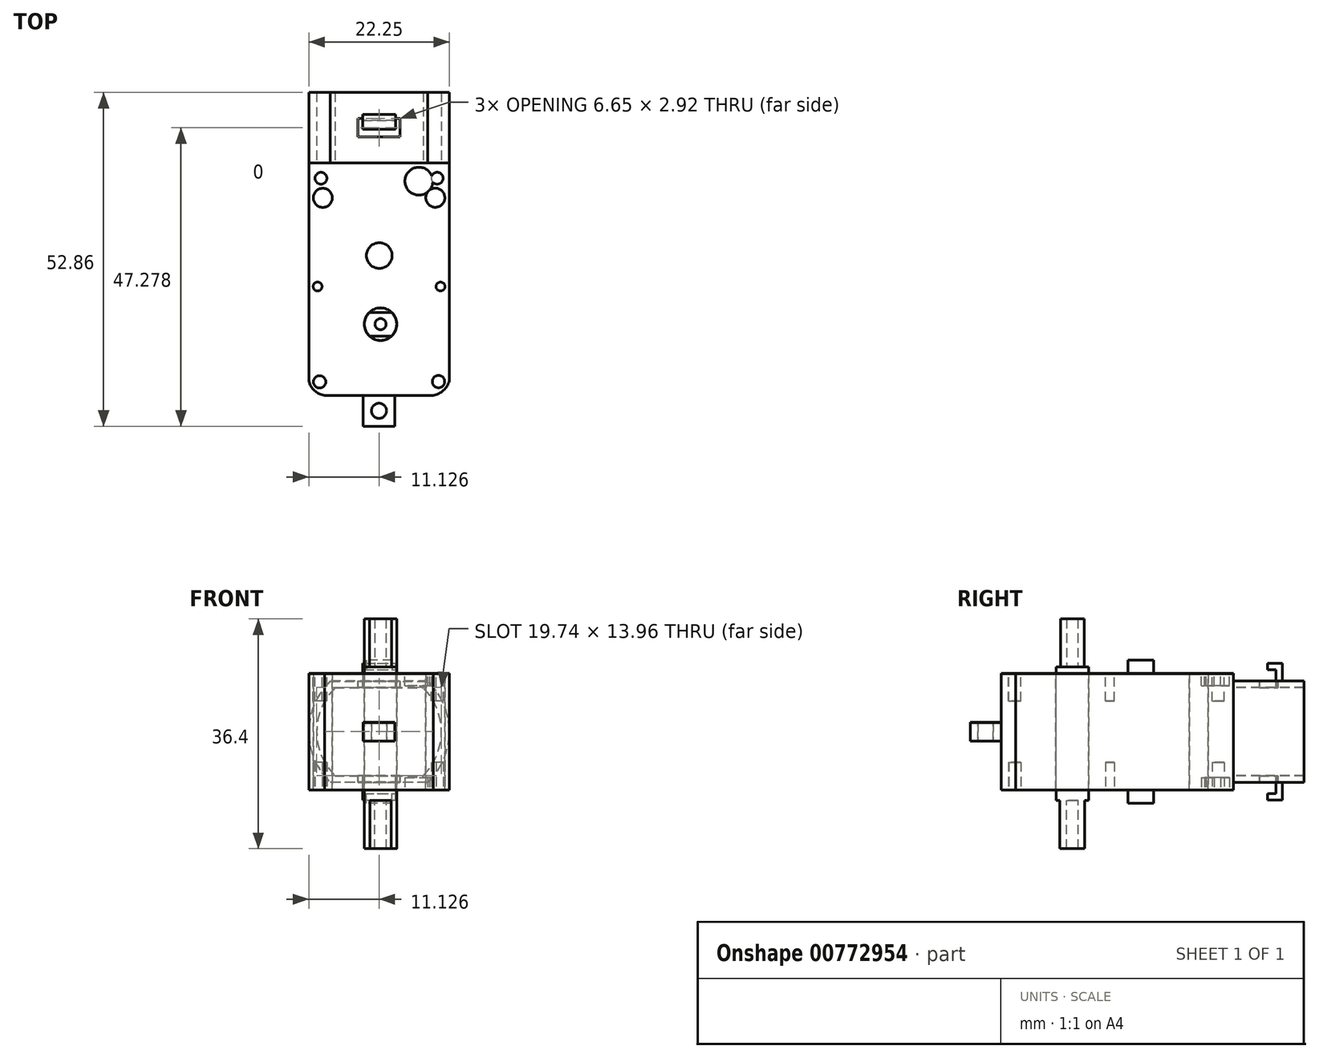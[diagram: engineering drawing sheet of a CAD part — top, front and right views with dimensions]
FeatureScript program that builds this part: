
annotation { "Feature Type Name" : "Feature", "Feature Type Description" : "" }
export const myFeature = defineFeature(function(context is Context, id is Id, definition is map)
    precondition{}
    {
        {
            var Q0;
            Q0=qCreatedBy(makeId("Top.planeOp"),FACE);
            var sketch = newSketch(context, id + "F0", { "sketchPlane" : qUnion([Q0])});
            skLineSegment(sketch, "E0.bottom", {"start": v(-45.26, 0.57) * mm, "end": v(-23, 0.57) * mm});
            skLineSegment(sketch, "E0.top", {"start": v(-42.73, -36.23) * mm, "end": v(-25.55, -36.23) * mm});
            skLineSegment(sketch, "E0.left", {"start": v(-45.26, 0.57) * mm, "end": v(-45.26, -33.94) * mm});
            skLineSegment(sketch, "E0.right", {"start": v(-23, 0.57) * mm, "end": v(-23, -33.94) * mm});
            skCircle(sketch, "E1", {"center": v(-25.23, -4.93) * mm, "radius": 1.51 * mm});
            skCircle(sketch, "E2", {"center": v(-43.04, -4.94) * mm, "radius": 1.51 * mm});
            skArc(sketch, "E3", {"start": v(-45.26, -33.94) * mm, "mid": v(-44.35, -35.48) * mm, "end": v(-42.73, -36.23) * mm});
            skArc(sketch, "E4", {"start": v(-25.55, -36.23) * mm, "mid": v(-23.95, -35.45) * mm, "end": v(-23, -33.94) * mm});
            skCircle(sketch, "E5", {"center": v(-33.9, -24.96) * mm, "radius": 2.58 * mm});
            skLineSegment(sketch, "E6", {"start": v(-25.39, -3.43) * mm, "end": v(-43.04, -3.43) * mm});
            skSolve(sketch);
        }
        {
            var Q0;
            Q0=makeQuery(id+"F0.imprint","IMPRINT",FACE,{"disambiguationData":[TD([[makeQuery(id+"F0.imprint","IMPRINT",EDGE,{"derivedFrom":sQuery(id+"F0.wireOp",EDGE,"E0.bottom")}),-1.0]])]});
            extrude(context, id + "F1", {"entities" : qUnion([Q0]), "depth" : 18.45 * mm, "offsetDistance" : 25.4 * mm});
        }
        {
            var Q0;
            Q0=makeQuery(id+"F1.opExtrude","CAP_FACE",FACE,{"disambiguationData":[OSD([sQuery(id+"F0.wireOp",EDGE,"E0.bottom"),sQuery(id+"F0.wireOp",EDGE,"E0.top"),sQuery(id+"F0.wireOp",EDGE,"E0.left"),sQuery(id+"F0.wireOp",EDGE,"E0.right"),sQuery(id+"F0.wireOp",EDGE,"E1"),sQuery(id+"F0.wireOp",EDGE,"E2"),sQuery(id+"F0.wireOp",EDGE,"E3"),sQuery(id+"F0.wireOp",EDGE,"E4"),sQuery(id+"F0.wireOp",EDGE,"E5")])],"isStart":false});
            var sketch = newSketch(context, id + "F2", { "sketchPlane" : qUnion([Q0])});
            skCircle(sketch, "E7", {"center": v(-34.1, -14.09) * mm, "radius": 2.03 * mm});
            skSolve(sketch);
        }
        {
            var Q0;
            Q0=makeQuery(id+"F2.imprint","IMPRINT",FACE,{"disambiguationData":[TD([[makeQuery(id+"F2.imprint","IMPRINT",EDGE,{"derivedFrom":sQuery(id+"F2.wireOp",EDGE,"E7")}),1.0]])]});
            extrude(context, id + "F3", {"entities" : qUnion([Q0]), "operationType" : NewBodyOperationType.ADD, "depth" : 2.08 * mm, "offsetDistance" : 25.4 * mm});
        }
        {
            var Q0;
            Q0=makeQuery(id+"F1.opExtrude","CAP_FACE",FACE,{"disambiguationData":[OSD([sQuery(id+"F0.wireOp",EDGE,"E0.bottom"),sQuery(id+"F0.wireOp",EDGE,"E0.top"),sQuery(id+"F0.wireOp",EDGE,"E0.left"),sQuery(id+"F0.wireOp",EDGE,"E0.right"),sQuery(id+"F0.wireOp",EDGE,"E1"),sQuery(id+"F0.wireOp",EDGE,"E2"),sQuery(id+"F0.wireOp",EDGE,"E3"),sQuery(id+"F0.wireOp",EDGE,"E4"),sQuery(id+"F0.wireOp",EDGE,"E5")])],"isStart":false});
            var sketch = newSketch(context, id + "F4", { "sketchPlane" : qUnion([Q0])});
            skCircle(sketch, "E8", {"center": v(-43.55, -34.1) * mm, "radius": 0.98 * mm});
            skCircle(sketch, "E9", {"center": v(-24.72, -34.04) * mm, "radius": 0.98 * mm});
            skCircle(sketch, "E10", {"center": v(-24.4, -19) * mm, "radius": 0.71 * mm});
            skCircle(sketch, "E11", {"center": v(-24.93, -1.84) * mm, "radius": 0.94 * mm});
            skCircle(sketch, "E12", {"center": v(-43.86, -19) * mm, "radius": 0.71 * mm});
            skCircle(sketch, "E13", {"center": v(-43.33, -1.84) * mm, "radius": 0.94 * mm});
            skCircle(sketch, "E14", {"center": v(-39.93, -1.7) * mm, "radius": 1.61 * mm});
            skCircle(sketch, "E15", {"center": v(-28.78, -0.73) * mm, "radius": 0.33 * mm});
            skSolve(sketch);
        }
        {
            var Q0;
            Q0=makeQuery(id+"F4.imprint","IMPRINT",FACE,{"disambiguationData":[TD([[makeQuery(id+"F4.imprint","IMPRINT",EDGE,{"derivedFrom":sQuery(id+"F4.wireOp",EDGE,"E13")}),1.0]])]});
            var Q1;
            Q1=makeQuery(id+"F4.imprint","IMPRINT",FACE,{"disambiguationData":[TD([[makeQuery(id+"F4.imprint","IMPRINT",EDGE,{"derivedFrom":sQuery(id+"F4.wireOp",EDGE,"E12")}),1.0]])]});
            var Q2;
            Q2=makeQuery(id+"F4.imprint","IMPRINT",FACE,{"disambiguationData":[TD([[makeQuery(id+"F4.imprint","IMPRINT",EDGE,{"derivedFrom":sQuery(id+"F4.wireOp",EDGE,"E8")}),1.0]])]});
            var Q3;
            Q3=makeQuery(id+"F4.imprint","IMPRINT",FACE,{"disambiguationData":[TD([[makeQuery(id+"F4.imprint","IMPRINT",EDGE,{"derivedFrom":sQuery(id+"F4.wireOp",EDGE,"E9")}),1.0]])]});
            var Q4;
            Q4=makeQuery(id+"F4.imprint","IMPRINT",FACE,{"disambiguationData":[TD([[makeQuery(id+"F4.imprint","IMPRINT",EDGE,{"derivedFrom":sQuery(id+"F4.wireOp",EDGE,"E10")}),1.0]])]});
            var Q5;
            Q5=makeQuery(id+"F4.imprint","IMPRINT",FACE,{"disambiguationData":[TD([[makeQuery(id+"F4.imprint","IMPRINT",EDGE,{"derivedFrom":sQuery(id+"F4.wireOp",EDGE,"E11")}),1.0]])]});
            extrude(context, id + "F5", {"entities" : qUnion([Q0, Q1, Q2, Q3, Q4, Q5]), "operationType" : NewBodyOperationType.REMOVE, "oppositeDirection" : true, "depth" : 4.4 * mm, "offsetDistance" : 25.4 * mm});
        }
        {
            var Q0;
            Q0=makeQuery(id+"F1.opExtrude","CAP_FACE",FACE,{"disambiguationData":[OSD([sQuery(id+"F0.wireOp",EDGE,"E0.bottom"),sQuery(id+"F0.wireOp",EDGE,"E0.top"),sQuery(id+"F0.wireOp",EDGE,"E0.left"),sQuery(id+"F0.wireOp",EDGE,"E0.right"),sQuery(id+"F0.wireOp",EDGE,"E1"),sQuery(id+"F0.wireOp",EDGE,"E2"),sQuery(id+"F0.wireOp",EDGE,"E3"),sQuery(id+"F0.wireOp",EDGE,"E4"),sQuery(id+"F0.wireOp",EDGE,"E5")])],"isStart":false});
            var sketch = newSketch(context, id + "F6", { "sketchPlane" : qUnion([Q0])});
            skCircle(sketch, "E16", {"center": v(-40.43, -2.3) * mm, "radius": 2.2 * mm});
            skCircle(sketch, "E17", {"center": v(-27.83, -2.3) * mm, "radius": 2.2 * mm});
            skSolve(sketch);
        }
        {
            var Q0;
            {var subQ0=sQuery(id+"F6.wireOp",EDGE,"E17");var subQ1=makeQuery(id+"F1.opExtrude","CAP_EDGE",EDGE,{"disambiguationData":[OSD([sQuery(id+"F0.wireOp",EDGE,"E1")])],"isStart":false});var subQ2=makeQuery(id+"F6.imprint","INTERSECT",VERTEX,{"disambiguationData":[OD(0.0)],"derivedFrom":[subQ1,subQ0]});Q0=makeQuery(id+"F6.imprint","IMPRINT",FACE,{"disambiguationData":[TD([[makeQuery(id+"F6.imprint","IMPRINT",EDGE,{"disambiguationData":[TD([[subQ2,1.0]])],"derivedFrom":subQ0}),1.0]])]});}
            var Q1;
            {var subQ0=sQuery(id+"F6.wireOp",EDGE,"E16");var subQ1=makeQuery(id+"F5.boolean.opBoolean","COPY",EDGE,{"derivedFrom":makeQuery(id+"F5.opExtrude","CAP_EDGE",EDGE,{"disambiguationData":[OSD([sQuery(id+"F4.wireOp",EDGE,"E13")])],"isStart":true})});var subQ2=makeQuery(id+"F6.imprint","INTERSECT",VERTEX,{"disambiguationData":[OD(0.0)],"derivedFrom":[subQ1,subQ0]});Q1=makeQuery(id+"F6.imprint","IMPRINT",FACE,{"disambiguationData":[TD([[makeQuery(id+"F6.imprint","IMPRINT",EDGE,{"disambiguationData":[TD([[subQ2,1.0]])],"derivedFrom":subQ0}),1.0]])]});}
            var Q2;
            {var subQ0=sQuery(id+"F6.wireOp",EDGE,"E16");var subQ1=makeQuery(id+"F1.opExtrude","CAP_EDGE",EDGE,{"disambiguationData":[OSD([sQuery(id+"F0.wireOp",EDGE,"E2")])],"isStart":false});var subQ2=makeQuery(id+"F6.imprint","INTERSECT",VERTEX,{"disambiguationData":[OD(0.0)],"derivedFrom":[subQ1,subQ0]});Q2=makeQuery(id+"F6.imprint","IMPRINT",FACE,{"disambiguationData":[TD([[makeQuery(id+"F6.imprint","IMPRINT",EDGE,{"disambiguationData":[TD([[subQ2,-1.0]])],"derivedFrom":subQ0}),1.0]])]});}
            var Q3;
            {var subQ0=sQuery(id+"F6.wireOp",EDGE,"E17");var subQ1=makeQuery(id+"F1.opExtrude","CAP_EDGE",EDGE,{"disambiguationData":[OSD([sQuery(id+"F0.wireOp",EDGE,"E1")])],"isStart":false});var subQ2=makeQuery(id+"F6.imprint","INTERSECT",VERTEX,{"disambiguationData":[OD(0.0)],"derivedFrom":[subQ1,subQ0]});Q3=makeQuery(id+"F6.imprint","IMPRINT",FACE,{"disambiguationData":[TD([[makeQuery(id+"F6.imprint","IMPRINT",EDGE,{"disambiguationData":[TD([[subQ2,-1.0]])],"derivedFrom":subQ0}),1.0]])]});}
            var Q4;
            {var subQ0=sQuery(id+"F6.wireOp",EDGE,"E17");var subQ1=makeQuery(id+"F5.boolean.opBoolean","COPY",EDGE,{"derivedFrom":makeQuery(id+"F5.opExtrude","CAP_EDGE",EDGE,{"disambiguationData":[OSD([sQuery(id+"F4.wireOp",EDGE,"E11")])],"isStart":true})});var subQ2=makeQuery(id+"F6.imprint","INTERSECT",VERTEX,{"disambiguationData":[OD(0.0)],"derivedFrom":[subQ1,subQ0]});Q4=makeQuery(id+"F6.imprint","IMPRINT",FACE,{"disambiguationData":[TD([[makeQuery(id+"F6.imprint","IMPRINT",EDGE,{"disambiguationData":[TD([[subQ2,1.0]])],"derivedFrom":subQ0}),1.0]])]});}
            var Q5;
            {var subQ0=sQuery(id+"F6.wireOp",EDGE,"E16");var subQ1=makeQuery(id+"F5.boolean.opBoolean","COPY",EDGE,{"derivedFrom":makeQuery(id+"F5.opExtrude","CAP_EDGE",EDGE,{"disambiguationData":[OSD([sQuery(id+"F4.wireOp",EDGE,"E13")])],"isStart":true})});var subQ2=makeQuery(id+"F6.imprint","INTERSECT",VERTEX,{"disambiguationData":[OD(0.0)],"derivedFrom":[subQ1,subQ0]});Q5=makeQuery(id+"F6.imprint","IMPRINT",FACE,{"disambiguationData":[TD([[makeQuery(id+"F6.imprint","IMPRINT",EDGE,{"disambiguationData":[TD([[subQ2,-1.0]])],"derivedFrom":subQ0}),1.0]])]});}
            extrude(context, id + "F7", {"entities" : qUnion([Q0, Q1, Q2, Q3, Q4, Q5]), "operationType" : NewBodyOperationType.REMOVE, "oppositeDirection" : true, "depth" : 1.98 * mm, "offsetDistance" : 25.4 * mm});
        }
        {
            var Q0;
            Q0=makeQuery(id+"F1.opExtrude","CAP_FACE",FACE,{"disambiguationData":[OSD([sQuery(id+"F0.wireOp",EDGE,"E0.bottom"),sQuery(id+"F0.wireOp",EDGE,"E0.top"),sQuery(id+"F0.wireOp",EDGE,"E0.left"),sQuery(id+"F0.wireOp",EDGE,"E0.right"),sQuery(id+"F0.wireOp",EDGE,"E1"),sQuery(id+"F0.wireOp",EDGE,"E2"),sQuery(id+"F0.wireOp",EDGE,"E3"),sQuery(id+"F0.wireOp",EDGE,"E4"),sQuery(id+"F0.wireOp",EDGE,"E5")])],"isStart":false});
            var sketch = newSketch(context, id + "F8", { "sketchPlane" : qUnion([Q0])});
            skCircle(sketch, "E18", {"center": v(-33.9, -24.96) * mm, "radius": 2.57 * mm});
            skSolve(sketch);
        }
        {
            var Q0;
            Q0 = qSketchRegion(id + "F8", true);
            extrude(context, id + "F9", {"entities" : qUnion([Q0]), "oppositeDirection" : true, "depth" : 18.47 * mm, "offsetDistance" : 25.4 * mm});
        }
        {
            var Q0;
            Q0 = qSketchRegion(id + "F8", true);
            var Q1;
            Q1=makeQuery(id+"F9.opExtrude","CAP_FACE",FACE,{"disambiguationData":[OSD([sQuery(id+"F8.wireOp",EDGE,"E18")])],"isStart":true});
            extrude(context, id + "F10", {"entities" : qUnion([Q0, Q1]), "depth" : 1.02 * mm, "offsetDistance" : 25.4 * mm});
        }
        {
            var Q0;
            {var subQ0=sQuery(id+"F8.wireOp",EDGE,"E18");Q0=makeQuery(id+"F10.opExtrude","CAP_FACE",FACE,{"disambiguationData":[OSD([subQ0]),TDD([makeQuery(id+"F8.imprint","IMPRINT",EDGE,{"derivedFrom":subQ0})])],"isStart":false});}
            var sketch = newSketch(context, id + "F11", { "sketchPlane" : qUnion([Q0])});
            skArc(sketch, "E19", {"start": v(-35.64, -23.09) * mm, "mid": v(-36.45, -24.96) * mm, "end": v(-35.64, -26.82) * mm});
            skLineSegment(sketch, "E20", {"start": v(-35.67, -23.09) * mm, "end": v(-32.13, -23.09) * mm});
            skLineSegment(sketch, "E21", {"start": v(-35.67, -26.82) * mm, "end": v(-32.16, -26.82) * mm});
            skArc(sketch, "E22.trimOffspring", {"start": v(-32.16, -26.82) * mm, "mid": v(-31.35, -24.96) * mm, "end": v(-32.16, -23.09) * mm});
            skCircle(sketch, "E23", {"center": v(-33.9, -24.96) * mm, "radius": 0.89 * mm});
            skSolve(sketch);
        }
        {
            var Q0;
            Q0=makeQuery(id+"F9.opExtrude","CAP_FACE",FACE,{"disambiguationData":[OSD([sQuery(id+"F8.wireOp",EDGE,"E18")])],"isStart":false});
            var sketch = newSketch(context, id + "F12", { "sketchPlane" : qUnion([Q0])});
            skCircle(sketch, "E24", {"center": v(-33.9, 24.96) * mm, "radius": 2.57 * mm});
            skSolve(sketch);
        }
        {
            var Q0;
            Q0=makeQuery(id+"F12.imprint","IMPRINT",FACE,{"disambiguationData":[TD([[makeQuery(id+"F12.imprint","IMPRINT",EDGE,{"derivedFrom":makeQuery(id+"F9.opExtrude","CAP_EDGE",EDGE,{"disambiguationData":[OSD([sQuery(id+"F8.wireOp",EDGE,"E18")])],"isStart":false})}),-1.0]])]});
            extrude(context, id + "F13", {"entities" : qUnion([Q0]), "operationType" : NewBodyOperationType.ADD, "depth" : 1.69 * mm, "offsetDistance" : 25.4 * mm});
        }
        {
            var Q0;
            Q0=makeQuery(id+"F1.opExtrude","SWEPT_FACE",FACE,{"disambiguationData":[OSD([sQuery(id+"F0.wireOp",EDGE,"E0.top")])]});
            var sketch = newSketch(context, id + "F14", { "sketchPlane" : qUnion([Q0])});
            skLineSegment(sketch, "E25.bottom", {"start": v(-42.65, 18.45) * mm, "end": v(-25.62, 18.45) * mm, "construction": true});
            skLineSegment(sketch, "E25.top", {"start": v(-42.65, 0) * mm, "end": v(-25.62, 0) * mm, "construction": true});
            skLineSegment(sketch, "E25.left", {"start": v(-42.65, 18.45) * mm, "end": v(-42.65, 0) * mm, "construction": true});
            skLineSegment(sketch, "E25.right", {"start": v(-25.62, 18.45) * mm, "end": v(-25.62, 0) * mm, "construction": true});
            skLineSegment(sketch, "E26", {"start": v(-34.14, 18.45) * mm, "end": v(-34.14, 0) * mm, "construction": true});
            skLineSegment(sketch, "E27", {"start": v(-42.65, 9.23) * mm, "end": v(-25.62, 9.23) * mm, "construction": true});
            skPoint(sketch, "E28", {"position": v(-34.14, 9.23) * mm});
            skLineSegment(sketch, "E29.bottom", {"start": v(-31.62, 7.75) * mm, "end": v(-36.65, 7.75) * mm});
            skLineSegment(sketch, "E29.top", {"start": v(-31.62, 10.7) * mm, "end": v(-36.65, 10.7) * mm});
            skLineSegment(sketch, "E29.left", {"start": v(-31.62, 7.75) * mm, "end": v(-31.62, 10.7) * mm});
            skLineSegment(sketch, "E29.right", {"start": v(-36.65, 7.75) * mm, "end": v(-36.65, 10.7) * mm});
            skSolve(sketch);
        }
        {
            var Q0;
            {var subQ2=sQuery(id+"F11.wireOp",EDGE,"E19");Q0=makeQuery(id+"F11.imprint","IMPRINT",FACE,{"disambiguationData":[TD([[makeQuery(id+"F11.imprint","IMPRINT",EDGE,{"derivedFrom":subQ2}),1.0]])]});}
            extrude(context, id + "F15", {"entities" : qUnion([Q0]), "depth" : 7.6 * mm, "offsetDistance" : 25.4 * mm});
        }
        {
            var Q0;
            Q0 = qSketchRegion(id + "F14", true);
            extrude(context, id + "F16", {"entities" : qUnion([Q0]), "operationType" : NewBodyOperationType.ADD, "depth" : 4.9 * mm, "offsetDistance" : 25.4 * mm});
        }
        {
            var Q0;
            Q0=makeQuery(id+"F13.opExtrude","CAP_FACE",FACE,{"disambiguationData":[OSD([sQuery(id+"F8.wireOp",EDGE,"E18")])],"isStart":false});
            var sketch = newSketch(context, id + "F17", { "sketchPlane" : qUnion([Q0])});
            skLineSegment(sketch, "E30", {"start": v(-35.56, 26.92) * mm, "end": v(-32.24, 26.92) * mm});
            skLineSegment(sketch, "E31", {"start": v(-35.55, 22.98) * mm, "end": v(-32.25, 22.98) * mm});
            skCircle(sketch, "E32", {"center": v(-33.9, 24.96) * mm, "radius": 0.93 * mm});
            skSolve(sketch);
        }
        {
            var Q0;
            Q0=makeQuery(id+"F16.opExtrude","SWEPT_FACE",FACE,{"disambiguationData":[OSD([sQuery(id+"F14.wireOp",EDGE,"E29.top")])]});
            var sketch = newSketch(context, id + "F18", { "sketchPlane" : qUnion([Q0])});
            skLineSegment(sketch, "E33.bottom", {"start": v(-36.65, -36.23) * mm, "end": v(-31.62, -36.23) * mm, "construction": true});
            skLineSegment(sketch, "E33.top", {"start": v(-36.65, -41.13) * mm, "end": v(-31.62, -41.13) * mm, "construction": true});
            skLineSegment(sketch, "E33.left", {"start": v(-36.65, -36.23) * mm, "end": v(-36.65, -41.13) * mm, "construction": true});
            skLineSegment(sketch, "E33.right", {"start": v(-31.62, -36.23) * mm, "end": v(-31.62, -41.13) * mm, "construction": true});
            skLineSegment(sketch, "E34", {"start": v(-34.14, -36.23) * mm, "end": v(-34.14, -41.13) * mm, "construction": true});
            skLineSegment(sketch, "E35", {"start": v(-36.65, -38.68) * mm, "end": v(-31.62, -38.68) * mm, "construction": true});
            skCircle(sketch, "E36", {"center": v(-34.14, -38.68) * mm, "radius": 1.2 * mm});
            skSolve(sketch);
        }
        {
            var Q0;
            Q0=makeQuery(id+"F18.imprint","IMPRINT",FACE,{"disambiguationData":[TD([[makeQuery(id+"F18.imprint","IMPRINT",EDGE,{"derivedFrom":sQuery(id+"F18.wireOp",EDGE,"E36")}),1.0]])]});
            var Q1;
            Q1=sQuery(id+"F18.wireOp",EDGE,"E36");
            extrude(context, id + "F19", {"entities" : qUnion([Q0]), "operationType" : NewBodyOperationType.REMOVE, "surfaceEntities" : qUnion([Q1]), "oppositeDirection" : true, "depth" : 25.4 * mm, "offsetDistance" : 25.4 * mm});
        }
        {
            var Q0;
            {var subQ0=sQuery(id+"F17.wireOp",EDGE,"E30");Q0=makeQuery(id+"F17.imprint","IMPRINT",FACE,{"disambiguationData":[TD([[makeQuery(id+"F17.imprint","IMPRINT",EDGE,{"derivedFrom":subQ0}),-1.0]])]});}
            extrude(context, id + "F20", {"entities" : qUnion([Q0]), "operationType" : NewBodyOperationType.ADD, "depth" : 7.62 * mm, "offsetDistance" : 25.4 * mm});
        }
        {
            var Q0;
            Q0=makeQuery(id+"F1.opExtrude","SWEPT_FACE",FACE,{"disambiguationData":[OSD([sQuery(id+"F0.wireOp",EDGE,"E0.bottom")])]});
            var sketch = newSketch(context, id + "F21", { "sketchPlane" : qUnion([Q0])});
            skArc(sketch, "E37", {"start": v(41.86, 1.22) * mm, "mid": v(45.26, 9.23) * mm, "end": v(41.86, 17.23) * mm});
            skLineSegment(sketch, "E38", {"start": v(39.9, 1.22) * mm, "end": v(28.37, 1.22) * mm});
            skLineSegment(sketch, "E39", {"start": v(39.9, 17.23) * mm, "end": v(28.37, 17.23) * mm});
            skArc(sketch, "E40.trimOffspring", {"start": v(26.41, 17.23) * mm, "mid": v(23, 9.23) * mm, "end": v(26.41, 1.22) * mm});
            skPoint(sketch, "E41.orphan", {"position": v(23, 17.23) * mm});
            skArc(sketch, "E42", {"start": v(41.11, 2.25) * mm, "mid": v(44, 9.23) * mm, "end": v(41.11, 16.2) * mm});
            skLineSegment(sketch, "E43", {"start": v(41.11, 2.25) * mm, "end": v(27.16, 2.25) * mm});
            skLineSegment(sketch, "E44", {"start": v(41.11, 16.2) * mm, "end": v(27.16, 16.2) * mm});
            skArc(sketch, "E45.trimOffspring", {"start": v(27.16, 16.2) * mm, "mid": v(24.27, 9.23) * mm, "end": v(27.16, 2.25) * mm});
            skLineSegment(sketch, "E46", {"start": v(39.9, 1.22) * mm, "end": v(41.86, 1.22) * mm});
            skLineSegment(sketch, "E47", {"start": v(28.37, 1.22) * mm, "end": v(26.41, 1.22) * mm});
            skLineSegment(sketch, "E48", {"start": v(26.41, 17.23) * mm, "end": v(28.37, 17.23) * mm});
            skLineSegment(sketch, "E49", {"start": v(39.9, 17.23) * mm, "end": v(41.86, 17.23) * mm});
            skSolve(sketch);
        }
        {
            var Q0;
            Q0=makeQuery(id+"F21.imprint","IMPRINT",FACE,{"disambiguationData":[TD([[makeQuery(id+"F21.imprint","IMPRINT",EDGE,{"derivedFrom":sQuery(id+"F21.wireOp",EDGE,"E38")}),-1.0]])]});
            extrude(context, id + "F22", {"entities" : qUnion([Q0]), "operationType" : NewBodyOperationType.ADD, "depth" : 11.16 * mm, "offsetDistance" : 25.4 * mm});
        }
        {
            var Q0;
            Q0=makeQuery(id+"F22.opExtrude","SWEPT_FACE",FACE,{"disambiguationData":[OSD([sQuery(id+"F21.wireOp",EDGE,"E39"),sQuery(id+"F21.wireOp",EDGE,"E48"),sQuery(id+"F21.wireOp",EDGE,"E49")])]});
            var sketch = newSketch(context, id + "F23", { "sketchPlane" : qUnion([Q0])});
            skLineSegment(sketch, "E50.bottom", {"start": v(-41.86, 11.73) * mm, "end": v(-26.41, 11.73) * mm, "construction": true});
            skLineSegment(sketch, "E50.top", {"start": v(-41.86, 0.57) * mm, "end": v(-26.41, 0.57) * mm, "construction": true});
            skLineSegment(sketch, "E50.left", {"start": v(-41.86, 11.73) * mm, "end": v(-41.86, 0.57) * mm, "construction": true});
            skLineSegment(sketch, "E50.right", {"start": v(-26.41, 11.73) * mm, "end": v(-26.41, 0.57) * mm, "construction": true});
            skLineSegment(sketch, "E51", {"start": v(-41.86, 6.15) * mm, "end": v(-26.41, 6.15) * mm, "construction": true});
            skLineSegment(sketch, "E52", {"start": v(-34.13, 11.73) * mm, "end": v(-34.13, 0.57) * mm, "construction": true});
            skLineSegment(sketch, "E53.bottom", {"start": v(-37.46, 7.6) * mm, "end": v(-30.8, 7.6) * mm});
            skLineSegment(sketch, "E53.top", {"start": v(-37.46, 4.69) * mm, "end": v(-30.8, 4.69) * mm});
            skLineSegment(sketch, "E53.left", {"start": v(-37.46, 7.6) * mm, "end": v(-37.46, 4.69) * mm});
            skLineSegment(sketch, "E53.right", {"start": v(-30.8, 7.6) * mm, "end": v(-30.8, 4.69) * mm});
            skPoint(sketch, "E53.middle", {"position": v(-34.13, 6.15) * mm});
            skLineSegment(sketch, "E54", {"start": v(-30.8, 7.6) * mm, "end": v(-31.52, 7.6) * mm, "construction": true});
            skLineSegment(sketch, "E55", {"start": v(-37.46, 7.6) * mm, "end": v(-36.75, 7.6) * mm, "construction": true});
            skLineSegment(sketch, "E56.bottom", {"start": v(-31.52, 7.3) * mm, "end": v(-36.75, 7.3) * mm, "construction": true});
            skLineSegment(sketch, "E56.top", {"start": v(-31.52, 7.91) * mm, "end": v(-36.75, 7.91) * mm, "construction": true});
            skLineSegment(sketch, "E56.left", {"start": v(-31.52, 7.3) * mm, "end": v(-31.52, 7.91) * mm, "construction": true});
            skLineSegment(sketch, "E56.right", {"start": v(-36.75, 7.3) * mm, "end": v(-36.75, 7.91) * mm, "construction": true});
            skPoint(sketch, "E56.middle", {"position": v(-34.13, 7.6) * mm});
            skLineSegment(sketch, "E57", {"start": v(-36.75, 7.6) * mm, "end": v(-36.75, 7.3) * mm});
            skLineSegment(sketch, "E58", {"start": v(-31.52, 7.3) * mm, "end": v(-36.75, 7.3) * mm});
            skLineSegment(sketch, "E59", {"start": v(-31.52, 7.3) * mm, "end": v(-31.52, 7.6) * mm});
            skSolve(sketch);
        }
        {
            var Q0;
            Q0=makeQuery(id+"F23.imprint","IMPRINT",FACE,{"disambiguationData":[TD([[makeQuery(id+"F23.imprint","IMPRINT",EDGE,{"derivedFrom":sQuery(id+"F23.wireOp",EDGE,"E53.top")}),1.0]])]});
            extrude(context, id + "F24", {"entities" : qUnion([Q0]), "operationType" : NewBodyOperationType.REMOVE, "oppositeDirection" : true, "depth" : 25.4 * mm, "offsetDistance" : 25.4 * mm});
        }
        {
            var Q0;
            Q0=makeQuery(id+"F22.opExtrude","SWEPT_FACE",FACE,{"disambiguationData":[OSD([sQuery(id+"F21.wireOp",EDGE,"E39"),sQuery(id+"F21.wireOp",EDGE,"E48"),sQuery(id+"F21.wireOp",EDGE,"E49")])]});
            var sketch = newSketch(context, id + "F25", { "sketchPlane" : qUnion([Q0])});
            skLineSegment(sketch, "E60", {"start": v(-36.75, 7.6) * mm, "end": v(-31.52, 7.6) * mm, "construction": true});
            skLineSegment(sketch, "E61.bottom", {"start": v(-36.75, 7.6) * mm, "end": v(-31.53, 7.6) * mm});
            skLineSegment(sketch, "E62", {"start": v(-36.75, 7.6) * mm, "end": v(-36.75, 5.93) * mm, "construction": true});
            skLineSegment(sketch, "E63", {"start": v(-31.52, 7.6) * mm, "end": v(-31.52, 5.93) * mm, "construction": true});
            skLineSegment(sketch, "E64.bottom", {"start": v(-36.75, 5.93) * mm, "end": v(-31.52, 5.93) * mm});
            skLineSegment(sketch, "E64.top", {"start": v(-36.75, 8.3) * mm, "end": v(-31.52, 8.3) * mm});
            skLineSegment(sketch, "E64.left", {"start": v(-36.75, 5.93) * mm, "end": v(-36.75, 8.3) * mm});
            skLineSegment(sketch, "E64.right", {"start": v(-31.52, 5.93) * mm, "end": v(-31.52, 8.3) * mm});
            skSolve(sketch);
        }
        {
            var Q0;
            Q0 = qSketchRegion(id + "F25", true);
            var Q1;
            {var subQ2=sQuery(id+"F25.wireOp",EDGE,"E61.top");Q1=makeQuery(id+"F25.imprint","IMPRINT",FACE,{"disambiguationData":[TD([[makeQuery(id+"F25.imprint","IMPRINT",EDGE,{"derivedFrom":subQ2}),1.0]])]});}
            extrude(context, id + "F26", {"entities" : qUnion([Q0, Q1]), "operationType" : NewBodyOperationType.ADD, "depth" : 2.82 * mm, "offsetDistance" : 25.4 * mm});
        }
        {
            var Q0;
            Q0=makeQuery(id+"F26.opExtrude","SWEPT_FACE",FACE,{"disambiguationData":[OSD([sQuery(id+"F25.wireOp",EDGE,"E64.bottom")])]});
            var sketch = newSketch(context, id + "F27", { "sketchPlane" : qUnion([Q0])});
            skLineSegment(sketch, "E65.bottom", {"start": v(-36.75, 17.23) * mm, "end": v(-31.52, 17.23) * mm, "construction": true});
            skLineSegment(sketch, "E65.top", {"start": v(-36.75, 19.04) * mm, "end": v(-31.52, 19.04) * mm, "construction": true});
            skLineSegment(sketch, "E65.left", {"start": v(-36.75, 17.23) * mm, "end": v(-36.75, 19.04) * mm, "construction": true});
            skLineSegment(sketch, "E65.right", {"start": v(-31.52, 17.23) * mm, "end": v(-31.52, 19.04) * mm, "construction": true});
            skLineSegment(sketch, "E66.bottom", {"start": v(-36.75, 17.23) * mm, "end": v(-31.52, 17.23) * mm});
            skLineSegment(sketch, "E66.top", {"start": v(-36.75, 19.04) * mm, "end": v(-31.52, 19.04) * mm});
            skLineSegment(sketch, "E66.left", {"start": v(-36.75, 17.23) * mm, "end": v(-36.75, 19.04) * mm});
            skLineSegment(sketch, "E66.right", {"start": v(-31.52, 17.23) * mm, "end": v(-31.52, 19.04) * mm});
            skSolve(sketch);
        }
        {
            var Q0;
            Q0 = qSketchRegion(id + "F27", true);
            extrude(context, id + "F28", {"entities" : qUnion([Q0]), "operationType" : NewBodyOperationType.REMOVE, "oppositeDirection" : true, "depth" : 1.37 * mm, "offsetDistance" : 25.4 * mm});
        }
        {
            var Q0;
            Q0=makeQuery(id+"F26.opExtrude","CAP_FACE",FACE,{"disambiguationData":[OSD([sQuery(id+"F25.wireOp",EDGE,"E64.bottom"),sQuery(id+"F25.wireOp",EDGE,"E64.top"),sQuery(id+"F25.wireOp",EDGE,"E64.left"),sQuery(id+"F25.wireOp",EDGE,"E64.right")])],"isStart":false});
            cPlane(context, id + "F29", {"entities" : qUnion([Q0]), "cplaneType" : CPlaneType.OFFSET, "offset" : 10.85 * mm, "oppositeDirection" : true, "width" : 152.4 * mm, "height" : 152.4 * mm});
        }
        {
            var Q0;
            Q0=makeQuery(id+"F1.opExtrude","SWEPT_BODY",BODY,{"disambiguationData":[OSD([sQuery(id+"F0.wireOp",EDGE,"E0.bottom"),sQuery(id+"F0.wireOp",EDGE,"E0.top"),sQuery(id+"F0.wireOp",EDGE,"E0.left"),sQuery(id+"F0.wireOp",EDGE,"E0.right"),sQuery(id+"F0.wireOp",EDGE,"E1"),sQuery(id+"F0.wireOp",EDGE,"E2"),sQuery(id+"F0.wireOp",EDGE,"E3"),sQuery(id+"F0.wireOp",EDGE,"E4"),sQuery(id+"F0.wireOp",EDGE,"E5")])]});
            var Q1;
            Q1=qCreatedBy(id+"F29.planeOp",FACE);
            mirror(context, id + "F30", {"entities" : qUnion([Q0]), "mirrorPlane" : qUnion([Q1])});
        }
    });
